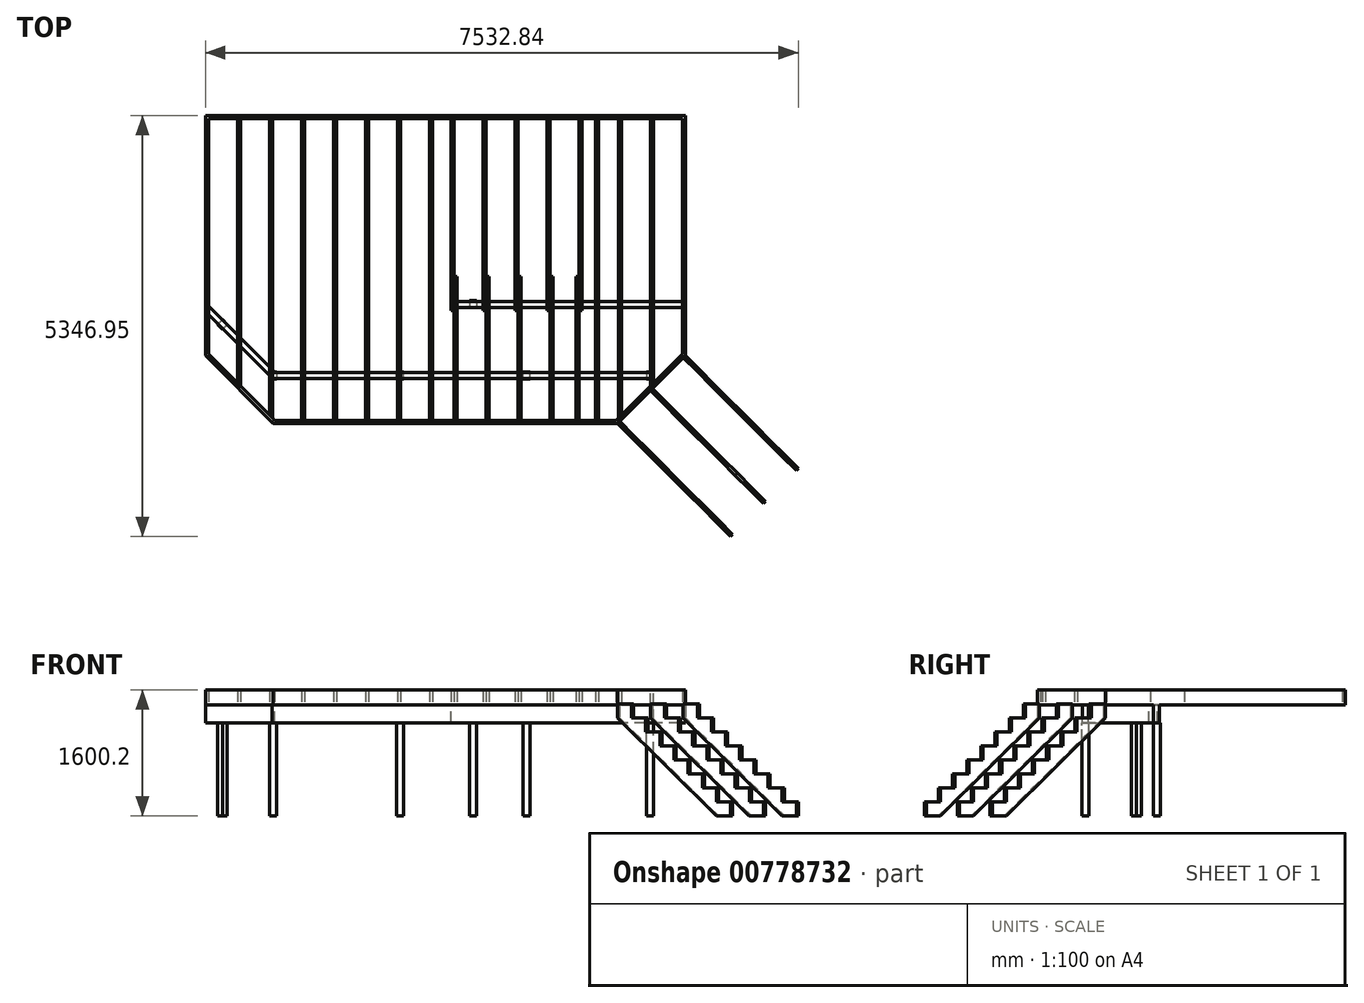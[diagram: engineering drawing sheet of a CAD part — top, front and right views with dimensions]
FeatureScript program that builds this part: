
annotation { "Feature Type Name" : "Feature", "Feature Type Description" : "" }
export const myFeature = defineFeature(function(context is Context, id is Id, definition is map)
    precondition{}
    {
        {
            var Q0;
            Q0=qCreatedBy(makeId("Top.planeOp"),FACE);
            var sketch = newSketch(context, id + "F0", { "sketchPlane" : qUnion([Q0])});
            skLineSegment(sketch, "E0.bottom", {"start": v(0, 0) * mm, "end": v(-6096, 0) * mm});
            skLineSegment(sketch, "E0.left", {"start": v(0, 0) * mm, "end": v(0, -3048) * mm});
            skLineSegment(sketch, "E0.right", {"start": v(-6096, 0) * mm, "end": v(-6096, -3048) * mm});
            skLineSegment(sketch, "E1", {"start": v(-6096, -3048) * mm, "end": v(-5233.9, -3910.1) * mm});
            skLineSegment(sketch, "E2", {"start": v(-5233.9, -3910.1) * mm, "end": v(-862.1, -3910.1) * mm});
            skLineSegment(sketch, "E3", {"start": v(-862.1, -3910.1) * mm, "end": v(0, -3048) * mm});
            skLineSegment(sketch, "E4", {"start": v(0, -2438.4) * mm, "end": v(-2743.2, -2438.4) * mm, "construction": true});
            skLineSegment(sketch, "E5.bottom", {"start": v(-2743.2, -2438.4) * mm, "end": v(-2654.3, -2438.4) * mm, "construction": true});
            skLineSegment(sketch, "E5.top", {"start": v(-2743.2, -2349.5) * mm, "end": v(-2654.3, -2349.5) * mm, "construction": true});
            skLineSegment(sketch, "E5.left", {"start": v(-2743.2, -2438.4) * mm, "end": v(-2743.2, -2349.5) * mm, "construction": true});
            skLineSegment(sketch, "E5.right", {"start": v(-2654.3, -2438.4) * mm, "end": v(-2654.3, -2349.5) * mm, "construction": true});
            skLineSegment(sketch, "E6", {"start": v(-406.4, 0) * mm, "end": v(-406.4, -3454.4) * mm, "construction": true});
            skLineSegment(sketch, "E7", {"start": v(-5233.9, -3300.5) * mm, "end": v(-3624.73, -3300.5) * mm, "construction": true});
            skLineSegment(sketch, "E8", {"start": v(-5233.9, -3300.5) * mm, "end": v(-6096, -2438.4) * mm, "construction": true});
            skLineSegment(sketch, "E9", {"start": v(-2015.57, -3300.5) * mm, "end": v(-406.4, -3300.5) * mm, "construction": true});
            skLineSegment(sketch, "E10", {"start": v(-3624.73, -3300.5) * mm, "end": v(-2015.57, -3300.5) * mm, "construction": true});
            skPoint(sketch, "E11", {"position": v(-5486.4, -3657.6) * mm});
            skPoint(sketch, "E12", {"position": v(-609.6, -3657.6) * mm});
            skSolve(sketch);
        }
        {
            var Q0;
            Q0=qCreatedBy(makeId("Top.planeOp"),FACE);
            var sketch = newSketch(context, id + "F1", { "sketchPlane" : qUnion([Q0])});
            skLineSegment(sketch, "E13.bottom", {"start": v(0, 0) * mm, "end": v(-2971.8, 0) * mm});
            skLineSegment(sketch, "E13.top", {"start": v(0, -38.1) * mm, "end": v(-2971.8, -38.1) * mm});
            skLineSegment(sketch, "E13.left", {"start": v(0, 0) * mm, "end": v(0, -38.1) * mm});
            skLineSegment(sketch, "E13.right", {"start": v(-2971.8, 0) * mm, "end": v(-2971.8, -38.1) * mm});
            skLineSegment(sketch, "E14.bottom", {"start": v(-2971.8, 0) * mm, "end": v(-6096, 0) * mm});
            skLineSegment(sketch, "E14.top", {"start": v(-2971.8, -38.1) * mm, "end": v(-6096, -38.1) * mm});
            skLineSegment(sketch, "E14.right", {"start": v(-6096, 0) * mm, "end": v(-6096, -38.1) * mm});
            skLineSegment(sketch, "E15.top", {"start": v(0, -3048) * mm, "end": v(-38.1, -3032.22) * mm});
            skLineSegment(sketch, "E15.left", {"start": v(0, -38.1) * mm, "end": v(0, -3048) * mm});
            skLineSegment(sketch, "E15.right", {"start": v(-38.1, -38.1) * mm, "end": v(-38.1, -3032.22) * mm});
            skLineSegment(sketch, "E16", {"start": v(0, -3048) * mm, "end": v(-862.1, -3910.1) * mm});
            skLineSegment(sketch, "E17", {"start": v(-862.1, -3910.1) * mm, "end": v(-5233.9, -3910.1) * mm});
            skLineSegment(sketch, "E18", {"start": v(-877.89, -3872) * mm, "end": v(-38.1, -3032.22) * mm});
            skLineSegment(sketch, "E19", {"start": v(-5233.9, -3910.1) * mm, "end": v(-6096, -3048) * mm});
            skLineSegment(sketch, "E20", {"start": v(-6096, -3048) * mm, "end": v(-6096, -38.1) * mm});
            skLineSegment(sketch, "E21", {"start": v(-877.89, -3872) * mm, "end": v(-5218.11, -3872) * mm});
            skLineSegment(sketch, "E22", {"start": v(-5218.11, -3872) * mm, "end": v(-6057.9, -3032.22) * mm});
            skLineSegment(sketch, "E23", {"start": v(-6057.9, -3032.22) * mm, "end": v(-6057.9, -38.1) * mm});
            skLineSegment(sketch, "E24", {"start": v(-6096, -3048) * mm, "end": v(-6057.9, -3032.22) * mm});
            skLineSegment(sketch, "E25", {"start": v(-5233.9, -3910.1) * mm, "end": v(-5218.11, -3872) * mm});
            skSolve(sketch);
        }
        {
            var Q0;
            Q0 = qSketchRegion(id + "F1", true);
            extrude(context, id + "F2", {"entities" : qUnion([Q0]), "depth" : 190.25 * mm, "offsetDistance" : 25.4 * mm});
        }
        {
            var Q0;
            Q0=qCreatedBy(makeId("Top.planeOp"),FACE);
            var sketch = newSketch(context, id + "F3", { "sketchPlane" : qUnion([Q0])});
            skLineSegment(sketch, "E26.bottom", {"start": v(-406.4, -34.38) * mm, "end": v(-444.5, -37.49) * mm});
            skLineSegment(sketch, "E26.left", {"start": v(-406.4, -34.38) * mm, "end": v(-406.4, -3400.52) * mm});
            skLineSegment(sketch, "E26.right", {"start": v(-444.5, -37.49) * mm, "end": v(-444.5, -3438.62) * mm});
            skLineSegment(sketch, "E27", {"start": v(-444.5, -3438.62) * mm, "end": v(-406.4, -3400.52) * mm});
            skLineSegment(sketch, "E28.bottom", {"start": v(-850.9, -38.1) * mm, "end": v(-812.8, -38.1) * mm});
            skLineSegment(sketch, "E28.left", {"start": v(-850.9, -38.1) * mm, "end": v(-850.9, -3845.02) * mm});
            skLineSegment(sketch, "E28.right", {"start": v(-812.8, -38.1) * mm, "end": v(-812.8, -3806.92) * mm});
            skLineSegment(sketch, "E29", {"start": v(-850.9, -3845.02) * mm, "end": v(-812.8, -3806.92) * mm});
            skLineSegment(sketch, "E30.bottom", {"start": v(-1104.9, -38.1) * mm, "end": v(-1143, -38.1) * mm});
            skLineSegment(sketch, "E30.top", {"start": v(-1104.9, -3872) * mm, "end": v(-1143, -3872) * mm});
            skLineSegment(sketch, "E30.left", {"start": v(-1104.9, -38.1) * mm, "end": v(-1104.9, -3872) * mm});
            skLineSegment(sketch, "E30.right", {"start": v(-1143, -38.1) * mm, "end": v(-1143, -3872) * mm});
            skLineSegment(sketch, "E31.bottom", {"start": v(-1352.55, -38.1) * mm, "end": v(-1314.45, -38.1) * mm});
            skLineSegment(sketch, "E31.top", {"start": v(-1352.55, -2476.5) * mm, "end": v(-1314.45, -2476.5) * mm});
            skLineSegment(sketch, "E31.left", {"start": v(-1352.55, -38.1) * mm, "end": v(-1352.55, -2476.5) * mm});
            skLineSegment(sketch, "E31.right", {"start": v(-1314.45, -38.1) * mm, "end": v(-1314.45, -2476.5) * mm});
            skLineSegment(sketch, "E32.bottom", {"start": v(-1720.85, -38.1) * mm, "end": v(-1758.95, -38.1) * mm});
            skLineSegment(sketch, "E32.top", {"start": v(-1720.85, -2476.5) * mm, "end": v(-1758.95, -2476.5) * mm});
            skLineSegment(sketch, "E32.left", {"start": v(-1720.85, -38.1) * mm, "end": v(-1720.85, -2476.5) * mm});
            skLineSegment(sketch, "E32.right", {"start": v(-1758.95, -38.1) * mm, "end": v(-1758.95, -2476.5) * mm});
            skLineSegment(sketch, "E33.bottom", {"start": v(-2127.25, -38.1) * mm, "end": v(-2165.35, -38.1) * mm});
            skLineSegment(sketch, "E33.top", {"start": v(-2127.25, -2476.5) * mm, "end": v(-2165.35, -2476.5) * mm});
            skLineSegment(sketch, "E33.left", {"start": v(-2127.25, -38.1) * mm, "end": v(-2127.25, -2476.5) * mm});
            skLineSegment(sketch, "E33.right", {"start": v(-2165.35, -38.1) * mm, "end": v(-2165.35, -2476.5) * mm});
            skLineSegment(sketch, "E34.bottom", {"start": v(-2533.65, -38.1) * mm, "end": v(-2571.75, -38.1) * mm});
            skLineSegment(sketch, "E34.top", {"start": v(-2533.65, -2476.5) * mm, "end": v(-2571.75, -2476.5) * mm});
            skLineSegment(sketch, "E34.left", {"start": v(-2533.65, -38.1) * mm, "end": v(-2533.65, -2476.5) * mm});
            skLineSegment(sketch, "E34.right", {"start": v(-2571.75, -38.1) * mm, "end": v(-2571.75, -2476.5) * mm});
            skLineSegment(sketch, "E35.bottom", {"start": v(-2940.05, -38.1) * mm, "end": v(-2978.15, -38.1) * mm});
            skLineSegment(sketch, "E35.top", {"start": v(-2940.05, -2476.5) * mm, "end": v(-2978.15, -2476.5) * mm});
            skLineSegment(sketch, "E35.left", {"start": v(-2940.05, -38.1) * mm, "end": v(-2940.05, -2476.5) * mm});
            skLineSegment(sketch, "E35.right", {"start": v(-2978.15, -38.1) * mm, "end": v(-2978.15, -2476.5) * mm});
            skSolve(sketch);
        }
        {
            var Q0;
            Q0 = qSketchRegion(id + "F3", true);
            extrude(context, id + "F4", {"entities" : qUnion([Q0]), "operationType" : NewBodyOperationType.ADD, "depth" : 190.75 * mm, "offsetDistance" : 25.4 * mm});
        }
        {
            var Q0;
            Q0=qCreatedBy(makeId("Top.planeOp"),FACE);
            var sketch = newSketch(context, id + "F5", { "sketchPlane" : qUnion([Q0])});
            skLineSegment(sketch, "E36.bottom", {"start": v(-5689.6, -38.1) * mm, "end": v(-5651.5, -38.1) * mm});
            skLineSegment(sketch, "E36.top", {"start": v(-5689.6, -3400.52) * mm, "end": v(-5651.5, -3438.62) * mm});
            skLineSegment(sketch, "E36.left", {"start": v(-5689.6, -38.1) * mm, "end": v(-5689.6, -3400.52) * mm});
            skLineSegment(sketch, "E36.right", {"start": v(-5651.5, -38.1) * mm, "end": v(-5651.5, -3438.62) * mm});
            skLineSegment(sketch, "E37.bottom", {"start": v(-5283.2, -38.1) * mm, "end": v(-5245.1, -38.1) * mm});
            skLineSegment(sketch, "E37.top", {"start": v(-5283.2, -3806.92) * mm, "end": v(-5245.1, -3845.02) * mm});
            skLineSegment(sketch, "E37.left", {"start": v(-5283.2, -38.1) * mm, "end": v(-5283.2, -3806.92) * mm});
            skLineSegment(sketch, "E37.right", {"start": v(-5245.1, -38.1) * mm, "end": v(-5245.1, -3845.02) * mm});
            skLineSegment(sketch, "E38.bottom", {"start": v(-4876.8, -38.1) * mm, "end": v(-4838.7, -38.1) * mm});
            skLineSegment(sketch, "E38.top", {"start": v(-4876.8, -3872) * mm, "end": v(-4838.7, -3872) * mm});
            skLineSegment(sketch, "E38.left", {"start": v(-4876.8, -38.1) * mm, "end": v(-4876.8, -3872) * mm});
            skLineSegment(sketch, "E38.right", {"start": v(-4838.7, -38.1) * mm, "end": v(-4838.7, -3872) * mm});
            skLineSegment(sketch, "E39.bottom", {"start": v(-4470.4, -38.1) * mm, "end": v(-4432.3, -38.1) * mm});
            skLineSegment(sketch, "E39.top", {"start": v(-4470.4, -3872) * mm, "end": v(-4432.3, -3872) * mm});
            skLineSegment(sketch, "E39.left", {"start": v(-4470.4, -38.1) * mm, "end": v(-4470.4, -3872) * mm});
            skLineSegment(sketch, "E39.right", {"start": v(-4432.3, -38.1) * mm, "end": v(-4432.3, -3872) * mm});
            skLineSegment(sketch, "E40.bottom", {"start": v(-4064, -38.1) * mm, "end": v(-4025.9, -38.1) * mm});
            skLineSegment(sketch, "E40.top", {"start": v(-4064, -3872) * mm, "end": v(-4025.9, -3872) * mm});
            skLineSegment(sketch, "E40.left", {"start": v(-4064, -38.1) * mm, "end": v(-4064, -3872) * mm});
            skLineSegment(sketch, "E40.right", {"start": v(-4025.9, -38.1) * mm, "end": v(-4025.9, -3872) * mm});
            skLineSegment(sketch, "E41.bottom", {"start": v(-3657.6, -38.1) * mm, "end": v(-3619.5, -38.1) * mm});
            skLineSegment(sketch, "E41.top", {"start": v(-3657.6, -3872) * mm, "end": v(-3619.5, -3872) * mm});
            skLineSegment(sketch, "E41.left", {"start": v(-3657.6, -38.1) * mm, "end": v(-3657.6, -3872) * mm});
            skLineSegment(sketch, "E41.right", {"start": v(-3619.5, -38.1) * mm, "end": v(-3619.5, -3872) * mm});
            skLineSegment(sketch, "E42.bottom", {"start": v(-3251.2, -38.1) * mm, "end": v(-3213.1, -38.1) * mm});
            skLineSegment(sketch, "E42.top", {"start": v(-3251.2, -3872) * mm, "end": v(-3213.1, -3872) * mm});
            skLineSegment(sketch, "E42.left", {"start": v(-3251.2, -38.1) * mm, "end": v(-3251.2, -3872) * mm});
            skLineSegment(sketch, "E42.right", {"start": v(-3213.1, -38.1) * mm, "end": v(-3213.1, -3872) * mm});
            skLineSegment(sketch, "E43.bottom", {"start": v(-2940.05, -3872) * mm, "end": v(-2901.95, -3872) * mm});
            skLineSegment(sketch, "E43.top", {"start": v(-2940.05, -2043.2) * mm, "end": v(-2901.95, -2043.2) * mm});
            skLineSegment(sketch, "E43.left", {"start": v(-2940.05, -3872) * mm, "end": v(-2940.05, -2043.2) * mm});
            skLineSegment(sketch, "E43.right", {"start": v(-2901.95, -3872) * mm, "end": v(-2901.95, -2043.2) * mm});
            skLineSegment(sketch, "E44.bottom", {"start": v(-2533.65, -3872) * mm, "end": v(-2495.55, -3872) * mm});
            skLineSegment(sketch, "E44.top", {"start": v(-2533.65, -2043.2) * mm, "end": v(-2495.55, -2043.2) * mm});
            skLineSegment(sketch, "E44.left", {"start": v(-2533.65, -3872) * mm, "end": v(-2533.65, -2043.2) * mm});
            skLineSegment(sketch, "E44.right", {"start": v(-2495.55, -3872) * mm, "end": v(-2495.55, -2043.2) * mm});
            skLineSegment(sketch, "E45.bottom", {"start": v(-2127.25, -2043.2) * mm, "end": v(-2089.15, -2043.2) * mm});
            skLineSegment(sketch, "E45.top", {"start": v(-2127.25, -3872) * mm, "end": v(-2089.15, -3872) * mm});
            skLineSegment(sketch, "E45.left", {"start": v(-2127.25, -2043.2) * mm, "end": v(-2127.25, -3872) * mm});
            skLineSegment(sketch, "E45.right", {"start": v(-2089.15, -2043.2) * mm, "end": v(-2089.15, -3872) * mm});
            skLineSegment(sketch, "E46.bottom", {"start": v(-1720.85, -2043.2) * mm, "end": v(-1682.75, -2043.2) * mm});
            skLineSegment(sketch, "E46.top", {"start": v(-1720.85, -3872) * mm, "end": v(-1682.75, -3872) * mm});
            skLineSegment(sketch, "E46.left", {"start": v(-1720.85, -2043.2) * mm, "end": v(-1720.85, -3872) * mm});
            skLineSegment(sketch, "E46.right", {"start": v(-1682.75, -2043.2) * mm, "end": v(-1682.75, -3872) * mm});
            skLineSegment(sketch, "E47.bottom", {"start": v(-1390.65, -2043.2) * mm, "end": v(-1352.55, -2043.2) * mm});
            skLineSegment(sketch, "E47.top", {"start": v(-1390.65, -3872) * mm, "end": v(-1352.55, -3872) * mm});
            skLineSegment(sketch, "E47.left", {"start": v(-1390.65, -2043.2) * mm, "end": v(-1390.65, -3872) * mm});
            skLineSegment(sketch, "E47.right", {"start": v(-1352.55, -2043.2) * mm, "end": v(-1352.55, -3872) * mm});
            skSolve(sketch);
        }
        {
            var Q0;
            Q0 = qSketchRegion(id + "F5", true);
            extrude(context, id + "F6", {"entities" : qUnion([Q0]), "operationType" : NewBodyOperationType.ADD, "depth" : 190.5 * mm, "offsetDistance" : 25.4 * mm});
        }
        {
            var Q0;
            Q0=qCreatedBy(makeId("Top.planeOp"),FACE);
            var sketch = newSketch(context, id + "F7", { "sketchPlane" : qUnion([Q0])});
            skLineSegment(sketch, "E48.bottom", {"start": v(0, -2438.4) * mm, "end": v(-2978.15, -2438.4) * mm});
            skLineSegment(sketch, "E48.top", {"start": v(0, -2362.2) * mm, "end": v(-2978.15, -2362.2) * mm});
            skLineSegment(sketch, "E48.left", {"start": v(0, -2438.4) * mm, "end": v(0, -2362.2) * mm});
            skLineSegment(sketch, "E48.right", {"start": v(-2978.15, -2438.4) * mm, "end": v(-2978.15, -2362.2) * mm});
            skLineSegment(sketch, "E49.bottom", {"start": v(-406.4, -3262.4) * mm, "end": v(-5218.11, -3262.4) * mm});
            skLineSegment(sketch, "E49.top", {"start": v(-406.4, -3338.6) * mm, "end": v(-5249.68, -3338.6) * mm});
            skLineSegment(sketch, "E49.left", {"start": v(-406.4, -3338.6) * mm, "end": v(-406.4, -3262.4) * mm});
            skLineSegment(sketch, "E49.right", {"start": v(-5249.68, -3338.6) * mm, "end": v(-5218.11, -3262.4) * mm});
            skLineSegment(sketch, "E50", {"start": v(-5218.11, -3262.4) * mm, "end": v(-6096, -2384.52) * mm});
            skLineSegment(sketch, "E51", {"start": v(-6096, -2384.52) * mm, "end": v(-6096, -2492.28) * mm});
            skLineSegment(sketch, "E52", {"start": v(-6096, -2492.28) * mm, "end": v(-5249.68, -3338.6) * mm});
            skSolve(sketch);
        }
        {
            var Q0;
            Q0 = qSketchRegion(id + "F7", true);
            extrude(context, id + "F8", {"entities" : qUnion([Q0]), "operationType" : NewBodyOperationType.ADD, "oppositeDirection" : true, "depth" : 228.6 * mm, "offsetDistance" : 25.4 * mm});
        }
        {
            var Q0;
            Q0=makeQuery(id+"F2.opExtrude","CAP_VERTEX",VERTEX,{"disambiguationData":[OSD([sQuery(id+"F1.wireOp",EDGE,"E15.top"),sQuery(id+"F1.wireOp",EDGE,"E15.left"),sQuery(id+"F1.wireOp",EDGE,"E16")])],"isStart":false});
            var Q1;
            Q1=makeQuery(id+"F2.opExtrude","CAP_EDGE",EDGE,{"disambiguationData":[OSD([sQuery(id+"F1.wireOp",EDGE,"E16")])],"isStart":false});
            cPlane(context, id + "F9", {"entities" : qUnion([Q0, Q1]), "cplaneType" : CPlaneType.LINE_POINT, "offset" : 25.4 * mm, "width" : 152.4 * mm, "height" : 152.4 * mm});
        }
        {
            var Q0;
            Q0=qCreatedBy(id+"F9.planeOp",FACE);
            cPlane(context, id + "F10", {"entities" : qUnion([Q0]), "cplaneType" : CPlaneType.OFFSET, "offset" : 609.6 * mm, "width" : 152.4 * mm, "height" : 152.4 * mm});
        }
        {
            var Q0;
            Q0=qCreatedBy(id+"F9.planeOp",FACE);
            cPlane(context, id + "F11", {"entities" : qUnion([Q0]), "cplaneType" : CPlaneType.OFFSET, "offset" : 1219.2 * mm, "width" : 152.4 * mm, "height" : 152.4 * mm});
        }
        {
            var Q0;
            Q0=qCreatedBy(id+"F9.planeOp",FACE);
            var sketch = newSketch(context, id + "F12", { "sketchPlane" : qUnion([Q0])});
            skLineSegment(sketch, "E53", {"start": v(2155.26, 12.95) * mm, "end": v(2409.26, 12.95) * mm});
            skLineSegment(sketch, "E54", {"start": v(2409.26, 12.95) * mm, "end": v(2409.26, -164.85) * mm});
            skLineSegment(sketch, "E55", {"start": v(2155.26, 12.95) * mm, "end": v(2155.26, -165.8) * mm});
            skLineSegment(sketch, "E56", {"start": v(2155.26, -165.8) * mm, "end": v(3931.9, -1409.45) * mm});
            skLineSegment(sketch, "E57", {"start": v(2409.26, -164.85) * mm, "end": v(2663.26, -164.85) * mm});
            skLineSegment(sketch, "E58", {"start": v(2663.26, -164.85) * mm, "end": v(2663.26, -342.65) * mm});
            skLineSegment(sketch, "E59", {"start": v(2663.26, -342.65) * mm, "end": v(2917.26, -342.65) * mm});
            skLineSegment(sketch, "E60", {"start": v(2917.26, -342.65) * mm, "end": v(2917.26, -520.45) * mm});
            skLineSegment(sketch, "E61", {"start": v(2917.26, -520.45) * mm, "end": v(3171.26, -520.45) * mm});
            skLineSegment(sketch, "E62", {"start": v(3171.26, -520.45) * mm, "end": v(3171.26, -698.25) * mm});
            skLineSegment(sketch, "E63", {"start": v(3171.26, -698.25) * mm, "end": v(3425.26, -698.25) * mm});
            skLineSegment(sketch, "E64", {"start": v(3425.26, -698.25) * mm, "end": v(3425.26, -876.05) * mm});
            skLineSegment(sketch, "E65", {"start": v(3425.26, -876.05) * mm, "end": v(3679.26, -876.05) * mm});
            skLineSegment(sketch, "E66", {"start": v(3679.26, -876.05) * mm, "end": v(3679.26, -1053.85) * mm});
            skLineSegment(sketch, "E67", {"start": v(3679.26, -1053.85) * mm, "end": v(3933.26, -1053.85) * mm});
            skLineSegment(sketch, "E68", {"start": v(3933.26, -1053.85) * mm, "end": v(3933.26, -1231.65) * mm});
            skLineSegment(sketch, "E69", {"start": v(3933.26, -1231.65) * mm, "end": v(4187.26, -1231.65) * mm});
            skLineSegment(sketch, "E70", {"start": v(4187.26, -1231.65) * mm, "end": v(4187.26, -1409.45) * mm});
            skLineSegment(sketch, "E71", {"start": v(4187.26, -1409.45) * mm, "end": v(3931.9, -1409.45) * mm});
            skPoint(sketch, "E72", {"position": v(2155.26, 190.25) * mm});
            skSolve(sketch);
        }
        {
            var Q0;
            Q0 = qSketchRegion(id + "F12", true);
            extrude(context, id + "F13", {"entities" : qUnion([Q0]), "operationType" : NewBodyOperationType.ADD, "depth" : 38.1 * mm, "offsetDistance" : 25.4 * mm});
        }
        {
            var Q0;
            Q0=qCreatedBy(id+"F10.planeOp",FACE);
            var sketch = newSketch(context, id + "F14", { "sketchPlane" : qUnion([Q0])});
            skLineSegment(sketch, "E73", {"start": v(2155.26, 12.95) * mm, "end": v(2409.26, 12.95) * mm});
            skLineSegment(sketch, "E74", {"start": v(2409.26, 12.95) * mm, "end": v(2409.26, -164.85) * mm});
            skLineSegment(sketch, "E75", {"start": v(2155.26, 12.95) * mm, "end": v(2155.26, -165.8) * mm});
            skLineSegment(sketch, "E76", {"start": v(2155.26, -165.8) * mm, "end": v(3931.9, -1409.45) * mm});
            skLineSegment(sketch, "E77", {"start": v(2409.26, -164.85) * mm, "end": v(2663.26, -164.85) * mm});
            skLineSegment(sketch, "E78", {"start": v(2663.26, -164.85) * mm, "end": v(2663.26, -342.65) * mm});
            skLineSegment(sketch, "E79", {"start": v(2663.26, -342.65) * mm, "end": v(2917.26, -342.65) * mm});
            skLineSegment(sketch, "E80", {"start": v(2917.26, -342.65) * mm, "end": v(2917.26, -520.45) * mm});
            skLineSegment(sketch, "E81", {"start": v(2917.26, -520.45) * mm, "end": v(3171.26, -520.45) * mm});
            skLineSegment(sketch, "E82", {"start": v(3171.26, -520.45) * mm, "end": v(3171.26, -698.25) * mm});
            skLineSegment(sketch, "E83", {"start": v(3171.26, -698.25) * mm, "end": v(3425.26, -698.25) * mm});
            skLineSegment(sketch, "E84", {"start": v(3425.26, -698.25) * mm, "end": v(3425.26, -876.05) * mm});
            skLineSegment(sketch, "E85", {"start": v(3425.26, -876.05) * mm, "end": v(3679.26, -876.05) * mm});
            skLineSegment(sketch, "E86", {"start": v(3679.26, -876.05) * mm, "end": v(3679.26, -1053.85) * mm});
            skLineSegment(sketch, "E87", {"start": v(3679.26, -1053.85) * mm, "end": v(3933.26, -1053.85) * mm});
            skLineSegment(sketch, "E88", {"start": v(3933.26, -1053.85) * mm, "end": v(3933.26, -1231.65) * mm});
            skLineSegment(sketch, "E89", {"start": v(3933.26, -1231.65) * mm, "end": v(4187.26, -1231.65) * mm});
            skLineSegment(sketch, "E90", {"start": v(4187.26, -1231.65) * mm, "end": v(4187.26, -1409.45) * mm});
            skLineSegment(sketch, "E91", {"start": v(4187.26, -1409.45) * mm, "end": v(3931.9, -1409.45) * mm});
            skSolve(sketch);
        }
        {
            var Q0;
            Q0 = qSketchRegion(id + "F14", true);
            extrude(context, id + "F15", {"entities" : qUnion([Q0]), "operationType" : NewBodyOperationType.ADD, "depth" : 19.05 * mm, "offsetDistance" : 25.4 * mm, "hasSecondDirection" : true, "secondDirectionOppositeDirection" : true, "secondDirectionDepth" : 19.05 * mm});
        }
        {
            var Q0;
            Q0=qCreatedBy(id+"F11.planeOp",FACE);
            var sketch = newSketch(context, id + "F16", { "sketchPlane" : qUnion([Q0])});
            skLineSegment(sketch, "E92", {"start": v(2155.26, 12.95) * mm, "end": v(2409.26, 12.95) * mm});
            skLineSegment(sketch, "E93", {"start": v(2409.26, 12.95) * mm, "end": v(2409.26, -164.85) * mm});
            skLineSegment(sketch, "E94", {"start": v(2155.26, 12.95) * mm, "end": v(2155.26, -165.8) * mm});
            skLineSegment(sketch, "E95", {"start": v(2155.26, -165.8) * mm, "end": v(3931.9, -1409.45) * mm});
            skLineSegment(sketch, "E96", {"start": v(2409.26, -164.85) * mm, "end": v(2663.26, -164.85) * mm});
            skLineSegment(sketch, "E97", {"start": v(2663.26, -164.85) * mm, "end": v(2663.26, -342.65) * mm});
            skLineSegment(sketch, "E98", {"start": v(2663.26, -342.65) * mm, "end": v(2917.26, -342.65) * mm});
            skLineSegment(sketch, "E99", {"start": v(2917.26, -342.65) * mm, "end": v(2917.26, -520.45) * mm});
            skLineSegment(sketch, "E100", {"start": v(2917.26, -520.45) * mm, "end": v(3171.26, -520.45) * mm});
            skLineSegment(sketch, "E101", {"start": v(3171.26, -520.45) * mm, "end": v(3171.26, -698.25) * mm});
            skLineSegment(sketch, "E102", {"start": v(3171.26, -698.25) * mm, "end": v(3425.26, -698.25) * mm});
            skLineSegment(sketch, "E103", {"start": v(3425.26, -698.25) * mm, "end": v(3425.26, -876.05) * mm});
            skLineSegment(sketch, "E104", {"start": v(3425.26, -876.05) * mm, "end": v(3679.26, -876.05) * mm});
            skLineSegment(sketch, "E105", {"start": v(3679.26, -876.05) * mm, "end": v(3679.26, -1053.85) * mm});
            skLineSegment(sketch, "E106", {"start": v(3679.26, -1053.85) * mm, "end": v(3933.26, -1053.85) * mm});
            skLineSegment(sketch, "E107", {"start": v(3933.26, -1053.85) * mm, "end": v(3933.26, -1231.65) * mm});
            skLineSegment(sketch, "E108", {"start": v(3933.26, -1231.65) * mm, "end": v(4187.26, -1231.65) * mm});
            skLineSegment(sketch, "E109", {"start": v(4187.26, -1231.65) * mm, "end": v(4187.26, -1409.45) * mm});
            skLineSegment(sketch, "E110", {"start": v(4187.26, -1409.45) * mm, "end": v(3931.9, -1409.45) * mm});
            skSolve(sketch);
        }
        {
            var Q0;
            Q0 = qSketchRegion(id + "F16", true);
            extrude(context, id + "F17", {"entities" : qUnion([Q0]), "operationType" : NewBodyOperationType.ADD, "oppositeDirection" : true, "depth" : 38.1 * mm, "offsetDistance" : 25.4 * mm});
        }
        {
            var Q0;
            Q0=qCreatedBy(makeId("Top.planeOp"),FACE);
            var Q1;
            Q1 = qBodyType(qCreatedBy(id + "F19" ,EDGE), BodyType.WIRE);
            cPlane(context, id + "F18", {"entities" : qUnion([Q0, Q1]), "cplaneType" : CPlaneType.OFFSET, "offset" : 228.6 * mm, "oppositeDirection" : true, "width" : 152.4 * mm, "height" : 152.4 * mm});
        }
        {
            var Q0;
            Q0=qCreatedBy(id+"F18.planeOp",FACE);
            var sketch = newSketch(context, id + "F19", { "sketchPlane" : qUnion([Q0])});
            skLineSegment(sketch, "E111.bottom", {"start": v(-2743.2, -2349.5) * mm, "end": v(-2654.3, -2349.5) * mm});
            skLineSegment(sketch, "E111.top", {"start": v(-2743.2, -2438.4) * mm, "end": v(-2654.3, -2438.4) * mm});
            skLineSegment(sketch, "E111.left", {"start": v(-2743.2, -2349.5) * mm, "end": v(-2743.2, -2438.4) * mm});
            skLineSegment(sketch, "E111.right", {"start": v(-2654.3, -2349.5) * mm, "end": v(-2654.3, -2438.4) * mm});
            skLineSegment(sketch, "E112", {"start": v(-5880.47, -2591.06) * mm, "end": v(-5817.61, -2653.93) * mm});
            skLineSegment(sketch, "E113", {"start": v(-5817.61, -2653.93) * mm, "end": v(-5880.47, -2716.79) * mm});
            skLineSegment(sketch, "E114", {"start": v(-5880.47, -2716.79) * mm, "end": v(-5943.34, -2653.93) * mm});
            skLineSegment(sketch, "E115", {"start": v(-5943.34, -2653.93) * mm, "end": v(-5880.47, -2591.06) * mm});
            skPoint(sketch, "E116", {"position": v(-5911.9, -2622.5) * mm});
            skPoint(sketch, "E117", {"position": v(-5849.04, -2685.36) * mm});
            skLineSegment(sketch, "E118.bottom", {"start": v(-5189.45, -3256.05) * mm, "end": v(-5278.35, -3256.05) * mm});
            skLineSegment(sketch, "E118.top", {"start": v(-5189.45, -3344.95) * mm, "end": v(-5278.35, -3344.95) * mm});
            skLineSegment(sketch, "E118.left", {"start": v(-5189.45, -3256.05) * mm, "end": v(-5189.45, -3344.95) * mm});
            skLineSegment(sketch, "E118.right", {"start": v(-5278.35, -3256.05) * mm, "end": v(-5278.35, -3344.95) * mm});
            skPoint(sketch, "E119", {"position": v(-5233.9, -3256.05) * mm});
            skPoint(sketch, "E120", {"position": v(-5189.45, -3300.5) * mm});
            skPoint(sketch, "E121", {"position": v(-5849.04, -2622.5) * mm});
            skPoint(sketch, "E122", {"position": v(-5911.9, -2685.36) * mm});
            skLineSegment(sketch, "E123", {"start": v(-5911.9, -2685.36) * mm, "end": v(-5849.04, -2622.5) * mm, "construction": true});
            skLineSegment(sketch, "E124.bottom", {"start": v(-495.3, -3256.05) * mm, "end": v(-406.4, -3256.05) * mm});
            skLineSegment(sketch, "E124.top", {"start": v(-495.3, -3344.95) * mm, "end": v(-406.4, -3344.95) * mm});
            skLineSegment(sketch, "E124.left", {"start": v(-495.3, -3256.05) * mm, "end": v(-495.3, -3344.95) * mm});
            skLineSegment(sketch, "E124.right", {"start": v(-406.4, -3256.05) * mm, "end": v(-406.4, -3344.95) * mm});
            skPoint(sketch, "E125", {"position": v(-495.3, -3300.5) * mm});
            skLineSegment(sketch, "E126.bottom", {"start": v(-1971.12, -3344.95) * mm, "end": v(-2060.02, -3344.95) * mm});
            skLineSegment(sketch, "E126.top", {"start": v(-1971.12, -3256.05) * mm, "end": v(-2060.02, -3256.05) * mm});
            skLineSegment(sketch, "E126.left", {"start": v(-1971.12, -3344.95) * mm, "end": v(-1971.12, -3256.05) * mm});
            skLineSegment(sketch, "E126.right", {"start": v(-2060.02, -3344.95) * mm, "end": v(-2060.02, -3256.05) * mm});
            skPoint(sketch, "E127", {"position": v(-2015.57, -3256.05) * mm});
            skPoint(sketch, "E128", {"position": v(-1971.12, -3300.5) * mm});
            skLineSegment(sketch, "E129.bottom", {"start": v(-3580.28, -3344.95) * mm, "end": v(-3669.18, -3344.95) * mm});
            skLineSegment(sketch, "E129.top", {"start": v(-3580.28, -3256.05) * mm, "end": v(-3669.18, -3256.05) * mm});
            skLineSegment(sketch, "E129.left", {"start": v(-3580.28, -3344.95) * mm, "end": v(-3580.28, -3256.05) * mm});
            skLineSegment(sketch, "E129.right", {"start": v(-3669.18, -3344.95) * mm, "end": v(-3669.18, -3256.05) * mm});
            skPoint(sketch, "E130", {"position": v(-3624.73, -3256.05) * mm});
            skPoint(sketch, "E131", {"position": v(-3580.28, -3300.5) * mm});
            skPoint(sketch, "E132", {"position": v(-5880.47, -2653.93) * mm});
            skSolve(sketch);
        }
        {
            var Q0;
            Q0 = qSketchRegion(id + "F19", true);
            var Q1;
            Q1=makeQuery(id+"F15.opExtrude","SWEPT_FACE",FACE,{"disambiguationData":[OSD([sQuery(id+"F14.wireOp",EDGE,"E91")])]});
            extrude(context, id + "F20", {"entities" : qUnion([Q0]), "operationType" : NewBodyOperationType.ADD, "endBound" : BoundingType.UP_TO_SURFACE, "oppositeDirection" : true, "depth" : 1270 * mm, "endBoundEntityFace" : qUnion([Q1]), "offsetDistance" : 25.4 * mm});
        }
    });
